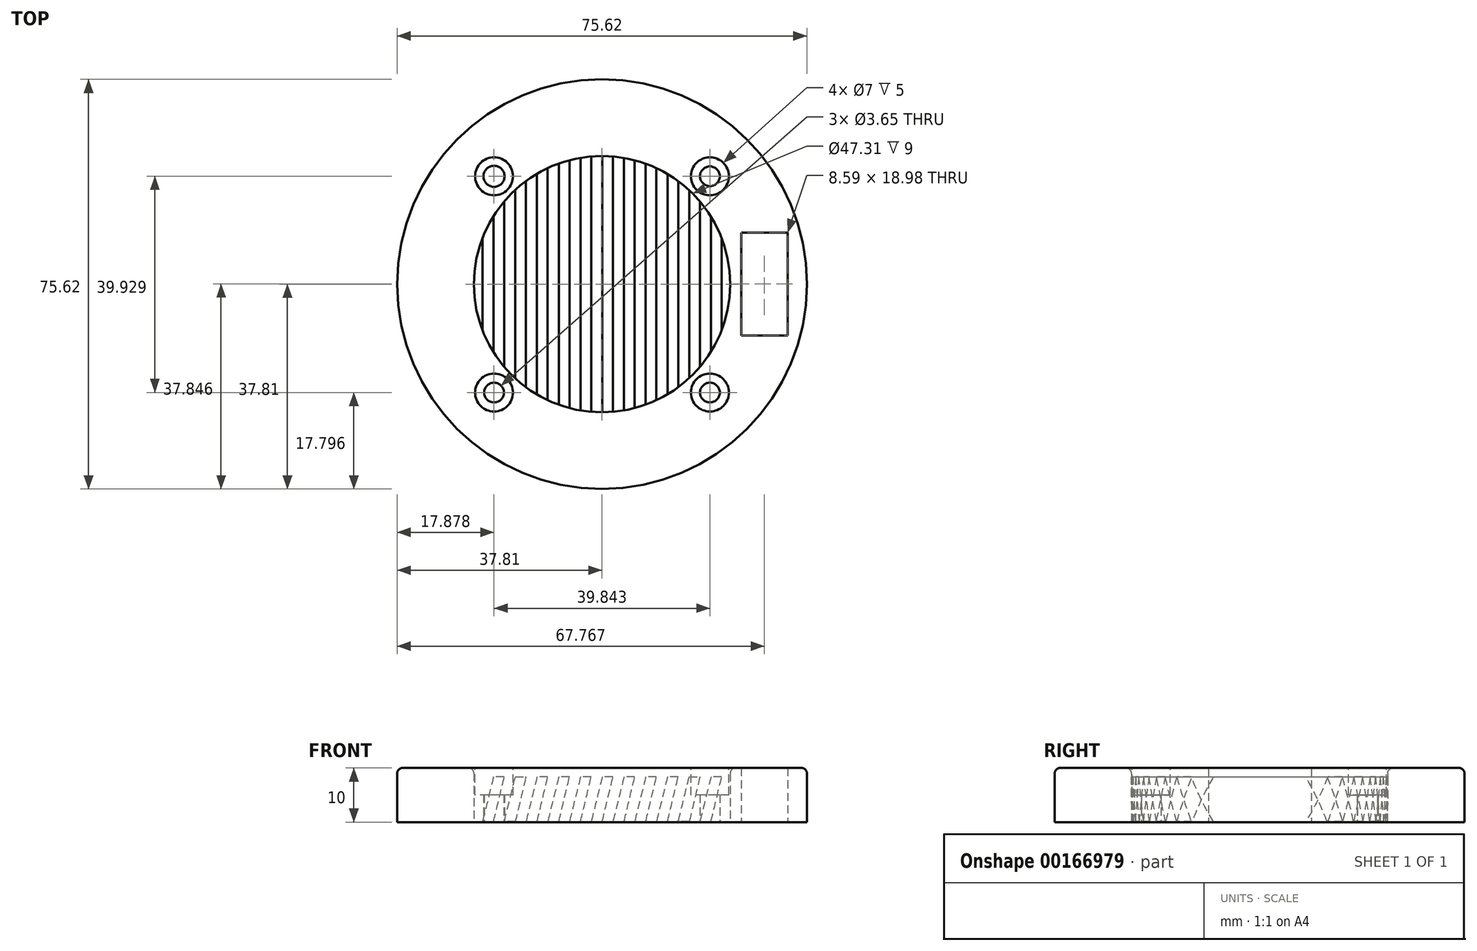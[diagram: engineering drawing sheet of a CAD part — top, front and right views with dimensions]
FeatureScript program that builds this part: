
annotation { "Feature Type Name" : "Feature", "Feature Type Description" : "" }
export const myFeature = defineFeature(function(context is Context, id is Id, definition is map)
    precondition{}
    {
        {
            var Q0;
            Q0=qCreatedBy(makeId("Top.planeOp"),FACE);
            var sketch = newSketch(context, id + "F0", { "sketchPlane" : qUnion([Q0])});
            skCircle(sketch, "E0", {"center": v(0, 0) * mm, "radius": 37.81 * mm});
            skCircle(sketch, "E1", {"center": v(-19.93, 19.91) * mm, "radius": 1.95 * mm});
            skCircle(sketch, "E2", {"center": v(-19.93, -20.01) * mm, "radius": 1.83 * mm});
            skCircle(sketch, "E3", {"center": v(19.91, -20.01) * mm, "radius": 1.83 * mm});
            skCircle(sketch, "E4", {"center": v(19.91, 19.91) * mm, "radius": 1.83 * mm});
            skCircle(sketch, "E5", {"center": v(0, 0) * mm, "radius": 23.65 * mm});
            skLineSegment(sketch, "E6.bottom", {"start": v(25.66, 9.52) * mm, "end": v(34.25, 9.52) * mm});
            skLineSegment(sketch, "E6.top", {"start": v(25.66, -9.45) * mm, "end": v(34.25, -9.45) * mm});
            skLineSegment(sketch, "E6.left", {"start": v(25.66, 9.52) * mm, "end": v(25.66, -9.45) * mm});
            skLineSegment(sketch, "E6.right", {"start": v(34.25, 9.52) * mm, "end": v(34.25, -9.45) * mm});
            skSolve(sketch);
        }
        {
            var Q0;
            Q0=makeQuery(id+"F0.imprint","IMPRINT",FACE,{"disambiguationData":[TD([[makeQuery(id+"F0.imprint","IMPRINT",EDGE,{"derivedFrom":sQuery(id+"F0.wireOp",EDGE,"E0")}),1.0]])]});
            extrude(context, id + "F1", {"entities" : qUnion([Q0]), "depth" : 10 * mm});
        }
        {
            var Q0;
            Q0=makeQuery(id+"F1.opExtrude","CAP_FACE",FACE,{"disambiguationData":[OSD([sQuery(id+"F0.wireOp",EDGE,"E0"),sQuery(id+"F0.wireOp",EDGE,"E1"),sQuery(id+"F0.wireOp",EDGE,"E2"),sQuery(id+"F0.wireOp",EDGE,"E3"),sQuery(id+"F0.wireOp",EDGE,"E4"),sQuery(id+"F0.wireOp",EDGE,"E5"),sQuery(id+"F0.wireOp",EDGE,"E6.bottom"),sQuery(id+"F0.wireOp",EDGE,"E6.top"),sQuery(id+"F0.wireOp",EDGE,"E6.left"),sQuery(id+"F0.wireOp",EDGE,"E6.right")])],"isStart":false});
            var sketch = newSketch(context, id + "F2", { "sketchPlane" : qUnion([Q0])});
            skCircle(sketch, "E7", {"center": v(-19.93, 19.91) * mm, "radius": 3.5 * mm});
            skCircle(sketch, "E8", {"center": v(19.91, 19.91) * mm, "radius": 3.5 * mm});
            skCircle(sketch, "E9", {"center": v(-19.93, -20.01) * mm, "radius": 3.5 * mm});
            skCircle(sketch, "E10", {"center": v(19.91, -20.01) * mm, "radius": 3.5 * mm});
            skSolve(sketch);
        }
        {
            var Q0;
            Q0=qCreatedBy(makeId("Front.planeOp"),FACE);
            var sketch = newSketch(context, id + "F3", { "sketchPlane" : qUnion([Q0])});
            skLineSegment(sketch, "E11", {"start": v(-2, 0.07) * mm, "end": v(0.04, 8.33) * mm});
            skLineSegment(sketch, "E12", {"start": v(0.04, 8.33) * mm, "end": v(2, 8.33) * mm});
            skLineSegment(sketch, "E13", {"start": v(2, 8.33) * mm, "end": v(0.04, 0.07) * mm});
            skLineSegment(sketch, "E14", {"start": v(0.04, 0.07) * mm, "end": v(-2, 0.07) * mm});
            skLineSegment(sketch, "E15", {"start": v(2, 0.07) * mm, "end": v(4.05, 8.33) * mm});
            skLineSegment(sketch, "E16", {"start": v(4.05, 8.33) * mm, "end": v(6.02, 8.33) * mm});
            skLineSegment(sketch, "E17", {"start": v(6.02, 8.33) * mm, "end": v(4.05, 0.07) * mm});
            skLineSegment(sketch, "E18", {"start": v(4.05, 0.07) * mm, "end": v(2, 0.07) * mm});
            skLineSegment(sketch, "E19", {"start": v(6.02, 0.07) * mm, "end": v(8.06, 8.33) * mm});
            skLineSegment(sketch, "E20", {"start": v(8.06, 8.33) * mm, "end": v(10.03, 8.33) * mm});
            skLineSegment(sketch, "E21", {"start": v(10.03, 8.33) * mm, "end": v(8.06, 0.07) * mm});
            skLineSegment(sketch, "E22", {"start": v(8.06, 0.07) * mm, "end": v(6.02, 0.07) * mm});
            skLineSegment(sketch, "E23", {"start": v(10.03, 0.07) * mm, "end": v(12.07, 8.33) * mm});
            skLineSegment(sketch, "E24", {"start": v(12.07, 8.33) * mm, "end": v(14.04, 8.33) * mm});
            skLineSegment(sketch, "E25", {"start": v(14.04, 8.33) * mm, "end": v(12.07, 0.07) * mm});
            skLineSegment(sketch, "E26", {"start": v(12.07, 0.07) * mm, "end": v(10.03, 0.07) * mm});
            skLineSegment(sketch, "E27", {"start": v(14.04, 0.07) * mm, "end": v(16.09, 8.33) * mm});
            skLineSegment(sketch, "E28", {"start": v(16.09, 8.33) * mm, "end": v(18.06, 8.33) * mm});
            skLineSegment(sketch, "E29", {"start": v(18.06, 8.33) * mm, "end": v(16.09, 0.07) * mm});
            skLineSegment(sketch, "E30", {"start": v(16.09, 0.07) * mm, "end": v(14.04, 0.07) * mm});
            skLineSegment(sketch, "E31", {"start": v(18.06, 0.07) * mm, "end": v(20.1, 8.33) * mm});
            skLineSegment(sketch, "E32", {"start": v(20.1, 8.33) * mm, "end": v(22.07, 8.33) * mm});
            skLineSegment(sketch, "E33", {"start": v(22.07, 8.33) * mm, "end": v(20.1, 0.07) * mm});
            skLineSegment(sketch, "E34", {"start": v(20.1, 0.07) * mm, "end": v(18.06, 0.07) * mm});
            skLineSegment(sketch, "E35", {"start": v(-6.02, 0.07) * mm, "end": v(-3.98, 8.33) * mm});
            skLineSegment(sketch, "E36", {"start": v(-3.98, 8.33) * mm, "end": v(-2, 8.33) * mm});
            skLineSegment(sketch, "E37", {"start": v(-2, 8.33) * mm, "end": v(-3.98, 0.07) * mm});
            skLineSegment(sketch, "E38", {"start": v(-3.98, 0.07) * mm, "end": v(-6.02, 0.07) * mm});
            skLineSegment(sketch, "E39", {"start": v(-10.03, 0.07) * mm, "end": v(-7.99, 8.33) * mm});
            skLineSegment(sketch, "E40", {"start": v(-7.99, 8.33) * mm, "end": v(-6.02, 8.33) * mm});
            skLineSegment(sketch, "E41", {"start": v(-6.02, 8.33) * mm, "end": v(-7.99, 0.07) * mm});
            skLineSegment(sketch, "E42", {"start": v(-7.99, 0.07) * mm, "end": v(-10.03, 0.07) * mm});
            skLineSegment(sketch, "E43", {"start": v(-14.04, 0.07) * mm, "end": v(-12, 8.33) * mm});
            skLineSegment(sketch, "E44", {"start": v(-12, 8.33) * mm, "end": v(-10.03, 8.33) * mm});
            skLineSegment(sketch, "E45", {"start": v(-10.03, 8.33) * mm, "end": v(-12, 0.07) * mm});
            skLineSegment(sketch, "E46", {"start": v(-12, 0.07) * mm, "end": v(-14.04, 0.07) * mm});
            skLineSegment(sketch, "E47", {"start": v(-18.06, 0.07) * mm, "end": v(-16.01, 8.33) * mm});
            skLineSegment(sketch, "E48", {"start": v(-16.01, 8.33) * mm, "end": v(-14.04, 8.33) * mm});
            skLineSegment(sketch, "E49", {"start": v(-14.04, 8.33) * mm, "end": v(-16.01, 0.07) * mm});
            skLineSegment(sketch, "E50", {"start": v(-16.01, 0.07) * mm, "end": v(-18.06, 0.07) * mm});
            skLineSegment(sketch, "E51", {"start": v(-22.07, 0.07) * mm, "end": v(-20.03, 8.33) * mm});
            skLineSegment(sketch, "E52", {"start": v(-20.03, 8.33) * mm, "end": v(-18.06, 8.33) * mm});
            skLineSegment(sketch, "E53", {"start": v(-18.06, 8.33) * mm, "end": v(-20.03, 0.07) * mm});
            skLineSegment(sketch, "E54", {"start": v(-20.03, 0.07) * mm, "end": v(-22.07, 0.07) * mm});
            skSolve(sketch);
        }
        {
            var Q0;
            Q0=makeQuery(id+"F3.imprint","IMPRINT",FACE,{"disambiguationData":[TD([[makeQuery(id+"F3.imprint","IMPRINT",EDGE,{"derivedFrom":sQuery(id+"F3.wireOp",EDGE,"E51")}),-1.0]])]});
            var Q1;
            Q1=makeQuery(id+"F3.imprint","IMPRINT",FACE,{"disambiguationData":[TD([[makeQuery(id+"F3.imprint","IMPRINT",EDGE,{"derivedFrom":sQuery(id+"F3.wireOp",EDGE,"E31")}),-1.0]])]});
            extrude(context, id + "F4", {"entities" : qUnion([Q0, Q1]), "operationType" : NewBodyOperationType.ADD, "endBound" : BoundingType.SYMMETRIC, "depth" : 31 * mm});
        }
        {
            var Q0;
            Q0=makeQuery(id+"F3.imprint","IMPRINT",FACE,{"disambiguationData":[TD([[makeQuery(id+"F3.imprint","IMPRINT",EDGE,{"derivedFrom":sQuery(id+"F3.wireOp",EDGE,"E47")}),-1.0]])]});
            var Q1;
            Q1=makeQuery(id+"F3.imprint","IMPRINT",FACE,{"disambiguationData":[TD([[makeQuery(id+"F3.imprint","IMPRINT",EDGE,{"derivedFrom":sQuery(id+"F3.wireOp",EDGE,"E27")}),-1.0]])]});
            extrude(context, id + "F5", {"entities" : qUnion([Q0, Q1]), "operationType" : NewBodyOperationType.ADD, "endBound" : BoundingType.SYMMETRIC, "depth" : 38 * mm});
        }
        {
            var Q0;
            Q0=makeQuery(id+"F3.imprint","IMPRINT",FACE,{"disambiguationData":[TD([[makeQuery(id+"F3.imprint","IMPRINT",EDGE,{"derivedFrom":sQuery(id+"F3.wireOp",EDGE,"E43")}),-1.0]])]});
            var Q1;
            Q1=makeQuery(id+"F3.imprint","IMPRINT",FACE,{"disambiguationData":[TD([[makeQuery(id+"F3.imprint","IMPRINT",EDGE,{"derivedFrom":sQuery(id+"F3.wireOp",EDGE,"E23")}),-1.0]])]});
            extrude(context, id + "F6", {"entities" : qUnion([Q0, Q1]), "operationType" : NewBodyOperationType.ADD, "endBound" : BoundingType.SYMMETRIC, "depth" : 44 * mm});
        }
        {
            var Q0;
            Q0=makeQuery(id+"F3.imprint","IMPRINT",FACE,{"disambiguationData":[TD([[makeQuery(id+"F3.imprint","IMPRINT",EDGE,{"derivedFrom":sQuery(id+"F3.wireOp",EDGE,"E39")}),-1.0]])]});
            var Q1;
            Q1=makeQuery(id+"F3.imprint","IMPRINT",FACE,{"disambiguationData":[TD([[makeQuery(id+"F3.imprint","IMPRINT",EDGE,{"derivedFrom":sQuery(id+"F3.wireOp",EDGE,"E19")}),-1.0]])]});
            extrude(context, id + "F7", {"entities" : qUnion([Q0, Q1]), "operationType" : NewBodyOperationType.ADD, "endBound" : BoundingType.SYMMETRIC, "depth" : 48 * mm});
        }
        {
            var Q0;
            Q0=makeQuery(id+"F3.imprint","IMPRINT",FACE,{"disambiguationData":[TD([[makeQuery(id+"F3.imprint","IMPRINT",EDGE,{"derivedFrom":sQuery(id+"F3.wireOp",EDGE,"E35")}),-1.0]])]});
            var Q1;
            Q1=makeQuery(id+"F3.imprint","IMPRINT",FACE,{"disambiguationData":[TD([[makeQuery(id+"F3.imprint","IMPRINT",EDGE,{"derivedFrom":sQuery(id+"F3.wireOp",EDGE,"E15")}),-1.0]])]});
            extrude(context, id + "F8", {"entities" : qUnion([Q0, Q1]), "operationType" : NewBodyOperationType.ADD, "endBound" : BoundingType.SYMMETRIC, "depth" : 55 * mm});
        }
        {
            var Q0;
            Q0=makeQuery(id+"F3.imprint","IMPRINT",FACE,{"disambiguationData":[TD([[makeQuery(id+"F3.imprint","IMPRINT",EDGE,{"derivedFrom":sQuery(id+"F3.wireOp",EDGE,"E11")}),-1.0]])]});
            extrude(context, id + "F9", {"entities" : qUnion([Q0]), "operationType" : NewBodyOperationType.ADD, "endBound" : BoundingType.SYMMETRIC, "depth" : 55 * mm});
        }
        {
            var Q0;
            Q0=makeQuery(id+"F2.imprint","IMPRINT",FACE,{"disambiguationData":[TD([[makeQuery(id+"F2.imprint","IMPRINT",EDGE,{"derivedFrom":sQuery(id+"F2.wireOp",EDGE,"E8")}),1.0]])]});
            var Q1;
            Q1=makeQuery(id+"F2.imprint","IMPRINT",FACE,{"disambiguationData":[TD([[makeQuery(id+"F2.imprint","IMPRINT",EDGE,{"derivedFrom":sQuery(id+"F2.wireOp",EDGE,"E9")}),1.0]])]});
            var Q2;
            Q2=makeQuery(id+"F2.imprint","IMPRINT",FACE,{"disambiguationData":[TD([[makeQuery(id+"F2.imprint","IMPRINT",EDGE,{"derivedFrom":sQuery(id+"F2.wireOp",EDGE,"E10")}),1.0]])]});
            var Q3;
            Q3=makeQuery(id+"F2.imprint","IMPRINT",FACE,{"disambiguationData":[TD([[makeQuery(id+"F2.imprint","IMPRINT",EDGE,{"derivedFrom":sQuery(id+"F2.wireOp",EDGE,"E7")}),1.0]])]});
            extrude(context, id + "F10", {"entities" : qUnion([Q0, Q1, Q2, Q3]), "operationType" : NewBodyOperationType.REMOVE, "oppositeDirection" : true, "depth" : 5 * mm});
        }
        {
            var Q0;
            Q0=makeQuery(id+"F1.opExtrude","CAP_EDGE",EDGE,{"disambiguationData":[OSD([sQuery(id+"F0.wireOp",EDGE,"E5")])],"isStart":false});
            var Q1;
            Q1=makeQuery(id+"F1.opExtrude","CAP_EDGE",EDGE,{"disambiguationData":[OSD([sQuery(id+"F0.wireOp",EDGE,"E0")])],"isStart":false});
            var Q2;
            Q2=makeQuery(id+"F10.boolean.opBoolean","COPY",EDGE,{"derivedFrom":makeQuery(id+"F10.opExtrude","CAP_EDGE",EDGE,{"disambiguationData":[OSD([sQuery(id+"F2.wireOp",EDGE,"E8")])],"isStart":true})});
            var Q3;
            Q3=makeQuery(id+"F10.boolean.opBoolean","COPY",EDGE,{"derivedFrom":makeQuery(id+"F10.opExtrude","CAP_EDGE",EDGE,{"disambiguationData":[OSD([sQuery(id+"F2.wireOp",EDGE,"E10")])],"isStart":true})});
            var Q4;
            Q4=makeQuery(id+"F10.boolean.opBoolean","COPY",EDGE,{"derivedFrom":makeQuery(id+"F10.opExtrude","CAP_EDGE",EDGE,{"disambiguationData":[OSD([sQuery(id+"F2.wireOp",EDGE,"E9")])],"isStart":true})});
            var Q5;
            Q5=makeQuery(id+"F10.boolean.opBoolean","COPY",EDGE,{"derivedFrom":makeQuery(id+"F10.opExtrude","CAP_EDGE",EDGE,{"disambiguationData":[OSD([sQuery(id+"F2.wireOp",EDGE,"E7")])],"isStart":true})});
            var Q6;
            Q6=makeQuery(id+"F10.boolean.opBoolean","COPY",EDGE,{"derivedFrom":makeQuery(id+"F10.opExtrude","CAP_EDGE",EDGE,{"disambiguationData":[OSD([sQuery(id+"F0.wireOp",EDGE,"E1")])],"isStart":false})});
            var Q7;
            Q7=makeQuery(id+"F10.boolean.opBoolean","COPY",EDGE,{"derivedFrom":makeQuery(id+"F10.opExtrude","CAP_EDGE",EDGE,{"disambiguationData":[OSD([sQuery(id+"F0.wireOp",EDGE,"E2")])],"isStart":false})});
            var Q8;
            Q8=makeQuery(id+"F10.boolean.opBoolean","COPY",EDGE,{"derivedFrom":makeQuery(id+"F10.opExtrude","CAP_EDGE",EDGE,{"disambiguationData":[OSD([sQuery(id+"F0.wireOp",EDGE,"E3")])],"isStart":false})});
            var Q9;
            Q9=makeQuery(id+"F10.boolean.opBoolean","COPY",EDGE,{"derivedFrom":makeQuery(id+"F10.opExtrude","CAP_EDGE",EDGE,{"disambiguationData":[OSD([sQuery(id+"F0.wireOp",EDGE,"E4")])],"isStart":false})});
            fillet(context, id + "F11", {"entities" : qUnion([Q0, Q1, Q2, Q3, Q4, Q5, Q6, Q7, Q8, Q9]), "radius" : 1 * mm, "tangentPropagation" : true, "allowEdgeOverflow" : false});
        }
    });
